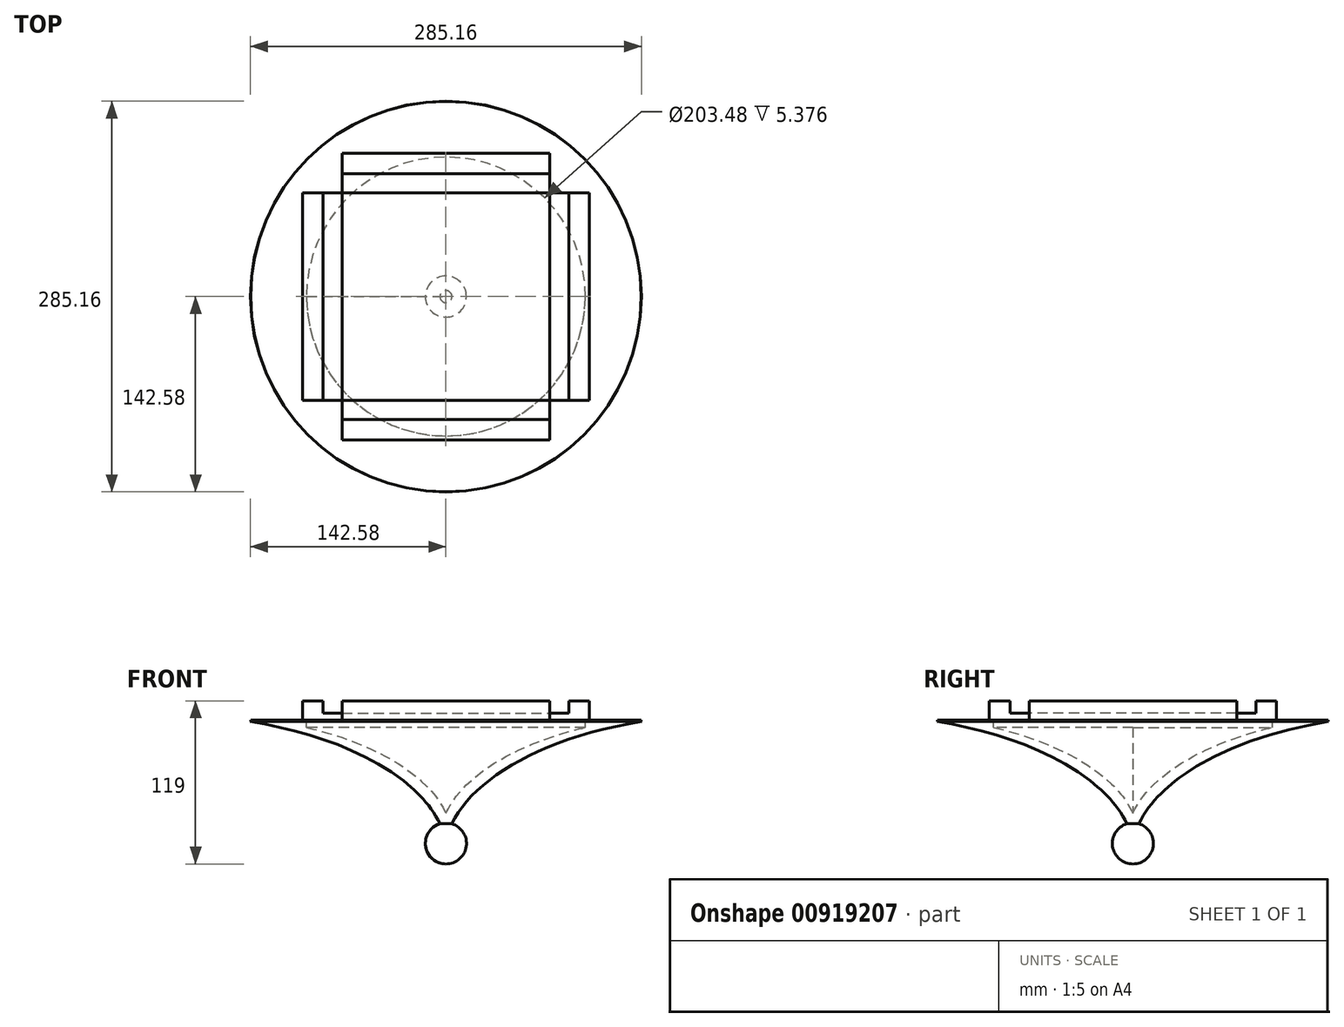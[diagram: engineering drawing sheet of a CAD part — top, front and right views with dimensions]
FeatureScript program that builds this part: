
annotation { "Feature Type Name" : "Feature", "Feature Type Description" : "" }
export const myFeature = defineFeature(function(context is Context, id is Id, definition is map)
    precondition{}
    {
        {
            var Q0;
            Q0=qCreatedBy(makeId("Top.planeOp"),FACE);
            var sketch = newSketch(context, id + "F0", { "sketchPlane" : qUnion([Q0])});
            skLineSegment(sketch, "E0.bottom", {"start": v(-104.75, 104.75) * mm, "end": v(104.75, 104.75) * mm});
            skLineSegment(sketch, "E0.top", {"start": v(-104.75, -104.75) * mm, "end": v(104.75, -104.75) * mm});
            skLineSegment(sketch, "E0.left", {"start": v(-104.75, 104.75) * mm, "end": v(-104.75, -104.75) * mm});
            skLineSegment(sketch, "E0.right", {"start": v(104.75, 104.75) * mm, "end": v(104.75, -104.75) * mm});
            skLineSegment(sketch, "E1.bottom", {"start": v(-75.75, 75.75) * mm, "end": v(75.75, 75.75) * mm});
            skLineSegment(sketch, "E1.top", {"start": v(-75.75, -75.75) * mm, "end": v(75.75, -75.75) * mm});
            skLineSegment(sketch, "E1.left", {"start": v(-75.75, 75.75) * mm, "end": v(-75.75, -75.75) * mm});
            skLineSegment(sketch, "E1.right", {"start": v(75.75, 75.75) * mm, "end": v(75.75, -75.75) * mm});
            skLineSegment(sketch, "E2.0", {"start": v(-89.75, 89.75) * mm, "end": v(-89.75, -89.75) * mm});
            skLineSegment(sketch, "E2.1", {"start": v(-89.75, 89.75) * mm, "end": v(89.75, 89.75) * mm});
            skLineSegment(sketch, "E2.2", {"start": v(89.75, 89.75) * mm, "end": v(89.75, -89.75) * mm});
            skLineSegment(sketch, "E2.3", {"start": v(-89.75, -89.75) * mm, "end": v(89.75, -89.75) * mm});
            skLineSegment(sketch, "E3.bottom", {"start": v(-75.75, 75.75) * mm, "end": v(-104.75, 75.75) * mm});
            skLineSegment(sketch, "E3.top", {"start": v(-75.75, 104.75) * mm, "end": v(-104.75, 104.75) * mm});
            skLineSegment(sketch, "E3.left", {"start": v(-75.75, 75.75) * mm, "end": v(-75.75, 104.75) * mm});
            skLineSegment(sketch, "E3.right", {"start": v(-104.75, 75.75) * mm, "end": v(-104.75, 104.75) * mm});
            skLineSegment(sketch, "E4.bottom", {"start": v(75.75, 75.75) * mm, "end": v(104.75, 75.75) * mm});
            skLineSegment(sketch, "E4.top", {"start": v(75.75, 104.75) * mm, "end": v(104.75, 104.75) * mm});
            skLineSegment(sketch, "E4.left", {"start": v(75.75, 75.75) * mm, "end": v(75.75, 104.75) * mm});
            skLineSegment(sketch, "E4.right", {"start": v(104.75, 75.75) * mm, "end": v(104.75, 104.75) * mm});
            skLineSegment(sketch, "E5.bottom", {"start": v(75.75, -75.75) * mm, "end": v(104.75, -75.75) * mm});
            skLineSegment(sketch, "E5.top", {"start": v(75.75, -104.75) * mm, "end": v(104.75, -104.75) * mm});
            skLineSegment(sketch, "E5.left", {"start": v(75.75, -75.75) * mm, "end": v(75.75, -104.75) * mm});
            skLineSegment(sketch, "E5.right", {"start": v(104.75, -75.75) * mm, "end": v(104.75, -104.75) * mm});
            skLineSegment(sketch, "E6.bottom", {"start": v(-75.75, -75.75) * mm, "end": v(-104.75, -75.75) * mm});
            skLineSegment(sketch, "E6.top", {"start": v(-75.75, -104.75) * mm, "end": v(-104.75, -104.75) * mm});
            skLineSegment(sketch, "E6.left", {"start": v(-75.75, -75.75) * mm, "end": v(-75.75, -104.75) * mm});
            skLineSegment(sketch, "E6.right", {"start": v(-104.75, -75.75) * mm, "end": v(-104.75, -104.75) * mm});
            skSolve(sketch);
        }
        {
            var Q0;
            Q0=makeQuery(id+"F0.imprint","IMPRINT",FACE,{"disambiguationData":[TD([[makeQuery(id+"F0.imprint","IMPRINT",EDGE,{"derivedFrom":sQuery(id+"F0.wireOp",EDGE,"E1.bottom")}),-1.0]])]});
            extrude(context, id + "F1", {"entities" : qUnion([Q0]), "depth" : 14 * mm, "offsetDistance" : 25 * mm});
        }
        {
            var Q0;
            Q0=makeQuery(id+"F0.imprint","IMPRINT",FACE,{"disambiguationData":[TD([[makeQuery(id+"F0.imprint","IMPRINT",EDGE,{"derivedFrom":sQuery(id+"F0.wireOp",EDGE,"E1.bottom")}),1.0]])]});
            var Q1;
            {var subQ0=sQuery(id+"F0.wireOp",EDGE,"E1.left");Q1=makeQuery(id+"F0.imprint","IMPRINT",FACE,{"disambiguationData":[TD([[makeQuery(id+"F0.imprint","IMPRINT",EDGE,{"derivedFrom":subQ0}),-1.0]])]});}
            var Q2;
            {var subQ0=sQuery(id+"F0.wireOp",EDGE,"E1.right");Q2=makeQuery(id+"F0.imprint","IMPRINT",FACE,{"disambiguationData":[TD([[makeQuery(id+"F0.imprint","IMPRINT",EDGE,{"derivedFrom":subQ0}),1.0]])]});}
            var Q3;
            {var subQ0=sQuery(id+"F0.wireOp",EDGE,"E1.top");Q3=makeQuery(id+"F0.imprint","IMPRINT",FACE,{"disambiguationData":[TD([[makeQuery(id+"F0.imprint","IMPRINT",EDGE,{"derivedFrom":subQ0}),-1.0]])]});}
            extrude(context, id + "F2", {"entities" : qUnion([Q0, Q1, Q2, Q3]), "operationType" : NewBodyOperationType.ADD, "depth" : 5 * mm, "offsetDistance" : 25 * mm});
        }
        {
            var Q0;
            {var subQ0=sQuery(id+"F0.wireOp",EDGE,"E0.left");Q0=makeQuery(id+"F0.imprint","IMPRINT",FACE,{"disambiguationData":[TD([[makeQuery(id+"F0.imprint","IMPRINT",EDGE,{"derivedFrom":subQ0}),1.0]])]});}
            var Q1;
            {var subQ0=sQuery(id+"F0.wireOp",EDGE,"E0.bottom");Q1=makeQuery(id+"F0.imprint","IMPRINT",FACE,{"disambiguationData":[TD([[makeQuery(id+"F0.imprint","IMPRINT",EDGE,{"derivedFrom":subQ0}),-1.0]])]});}
            var Q2;
            {var subQ0=sQuery(id+"F0.wireOp",EDGE,"E0.right");Q2=makeQuery(id+"F0.imprint","IMPRINT",FACE,{"disambiguationData":[TD([[makeQuery(id+"F0.imprint","IMPRINT",EDGE,{"derivedFrom":subQ0}),-1.0]])]});}
            var Q3;
            {var subQ0=sQuery(id+"F0.wireOp",EDGE,"E0.top");Q3=makeQuery(id+"F0.imprint","IMPRINT",FACE,{"disambiguationData":[TD([[makeQuery(id+"F0.imprint","IMPRINT",EDGE,{"derivedFrom":subQ0}),1.0]])]});}
            extrude(context, id + "F3", {"entities" : qUnion([Q0, Q1, Q2, Q3]), "operationType" : NewBodyOperationType.ADD, "depth" : 14 * mm, "offsetDistance" : 25 * mm});
        }
        {
            var Q0;
            Q0=qCreatedBy(makeId("Front.planeOp"),FACE);
            var sketch = newSketch(context, id + "F4", { "sketchPlane" : qUnion([Q0])});
            skLineSegment(sketch, "E7", {"start": v(0, 0) * mm, "end": v(-150, 0) * mm, "construction": true});
            skLineSegment(sketch, "E8", {"start": v(0, 0) * mm, "end": v(0, 90) * mm, "construction": true});
            skCircle(sketch, "E9", {"center": v(-150, 0) * mm, "radius": 7.5 * mm});
            skLineSegment(sketch, "E10.MirrorCS", {"start": v(0, -97.5) * mm, "end": v(0, -68.12) * mm});
            skLineSegment(sketch, "E11.MirrorCS", {"start": v(0, 0) * mm, "end": v(0, -90) * mm, "construction": true});
            skFitSpline(sketch, "E12.MirrorCS", {"points": [v(0, -90) * mm, v(-150, 0) * mm], "startDerivative": vector(-15.34, 110.8) * mm, "endDerivative": vector(-271.88, 38.4) * mm});
            skCircle(sketch, "E13.MirrorC", {"center": v(0, -90) * mm, "radius": 15 * mm});
            skFitSpline(sketch, "E14.MirrorCS", {"points": [v(-142.5, 0) * mm, v(4.6, -84.07) * mm], "startDerivative": vector(122.28, 0) * mm, "endDerivative": vector(21.97, -173.31) * mm});
            skLineSegment(sketch, "E15", {"start": v(-142.5, 0) * mm, "end": v(-101.74, 0) * mm});
            skLineSegment(sketch, "E16", {"start": v(-101.74, -5.38) * mm, "end": v(-101.74, 0) * mm});
            skLineSegment(sketch, "E17", {"start": v(0, -97.5) * mm, "end": v(0, -105) * mm});
            skSolve(sketch);
        }
        {
            var Q0;
            {var subQ0=sQuery(id+"F4.wireOp",EDGE,"E9");var subQ2=makeQuery(id+"F4.imprint","INTERSECT",VERTEX,{"derivedFrom":[sQuery(id+"F4.wireOp",EDGE,"E12.MirrorCS"),subQ0]});Q0=makeQuery(id+"F4.imprint","IMPRINT",FACE,{"disambiguationData":[TD([[makeQuery(id+"F4.imprint","IMPRINT",EDGE,{"disambiguationData":[TD([[subQ2,1.0]])],"derivedFrom":subQ0}),-1.0]])]});}
            var Q1;
            {var subQ0=sQuery(id+"F4.wireOp",EDGE,"E15");Q1=makeQuery(id+"F4.imprint","IMPRINT",FACE,{"disambiguationData":[TD([[makeQuery(id+"F4.imprint","IMPRINT",EDGE,{"derivedFrom":subQ0}),-1.0]])]});}
            var Q2;
            {var subQ3=sQuery(id+"F4.wireOp",EDGE,"E10.MirrorCS");var subQ5=sQuery(id+"F4.wireOp",EDGE,"E14.MirrorCS");var subQ9=makeQuery(id+"F4.imprint","INTERSECT",VERTEX,{"derivedFrom":[subQ3,subQ5]});Q2=makeQuery(id+"F4.imprint","IMPRINT",FACE,{"disambiguationData":[TD([[makeQuery(id+"F4.imprint","IMPRINT",EDGE,{"disambiguationData":[TD([[subQ9,1.0]])],"derivedFrom":subQ3}),1.0]])]});}
            var Q3;
            {var subQ0=sQuery(id+"F4.wireOp",EDGE,"E12.MirrorCS");var subQ1=sQuery(id+"F4.wireOp",EDGE,"E10.MirrorCS");var subQ2=makeQuery(id+"F4.imprint","INTERSECT",VERTEX,{"derivedFrom":[subQ1,subQ0]});Q3=makeQuery(id+"F4.imprint","IMPRINT",FACE,{"disambiguationData":[TD([[makeQuery(id+"F4.imprint","IMPRINT",EDGE,{"disambiguationData":[TD([[subQ2,-1.0]])],"derivedFrom":subQ1}),1.0]])]});}
            var Q4;
            {var subQ0=sQuery(id+"F4.wireOp",EDGE,"E13.MirrorC");var subQ1=sQuery(id+"F4.wireOp",EDGE,"E10.MirrorCS");var subQ2=makeQuery(id+"F4.imprint","INTERSECT",VERTEX,{"disambiguationData":[OD(0.0)],"derivedFrom":[subQ1,subQ0]});Q4=makeQuery(id+"F4.imprint","IMPRINT",FACE,{"disambiguationData":[TD([[makeQuery(id+"F4.imprint","IMPRINT",EDGE,{"disambiguationData":[TD([[subQ2,-1.0]])],"derivedFrom":subQ1}),1.0]])]});}
            var Q5;
            {var subQ0=sQuery(id+"F4.wireOp",EDGE,"E17");Q5=makeQuery(id+"F4.imprint","IMPRINT",FACE,{"disambiguationData":[TD([[makeQuery(id+"F4.imprint","IMPRINT",EDGE,{"derivedFrom":subQ0}),-1.0]])]});}
            var Q6;
            Q6=sQuery(id+"F4.wireOp",EDGE,"E11.MirrorCS");
            revolve(context, id + "F5", {"operationType" : NewBodyOperationType.ADD, "surfaceOperationType" : NewSurfaceOperationType.NEW, "entities" : qUnion([Q0, Q1, Q2, Q3, Q4, Q5]), "axis" : qUnion([Q6]), "revolveType" : RevolveType.FULL});
        }
    });
